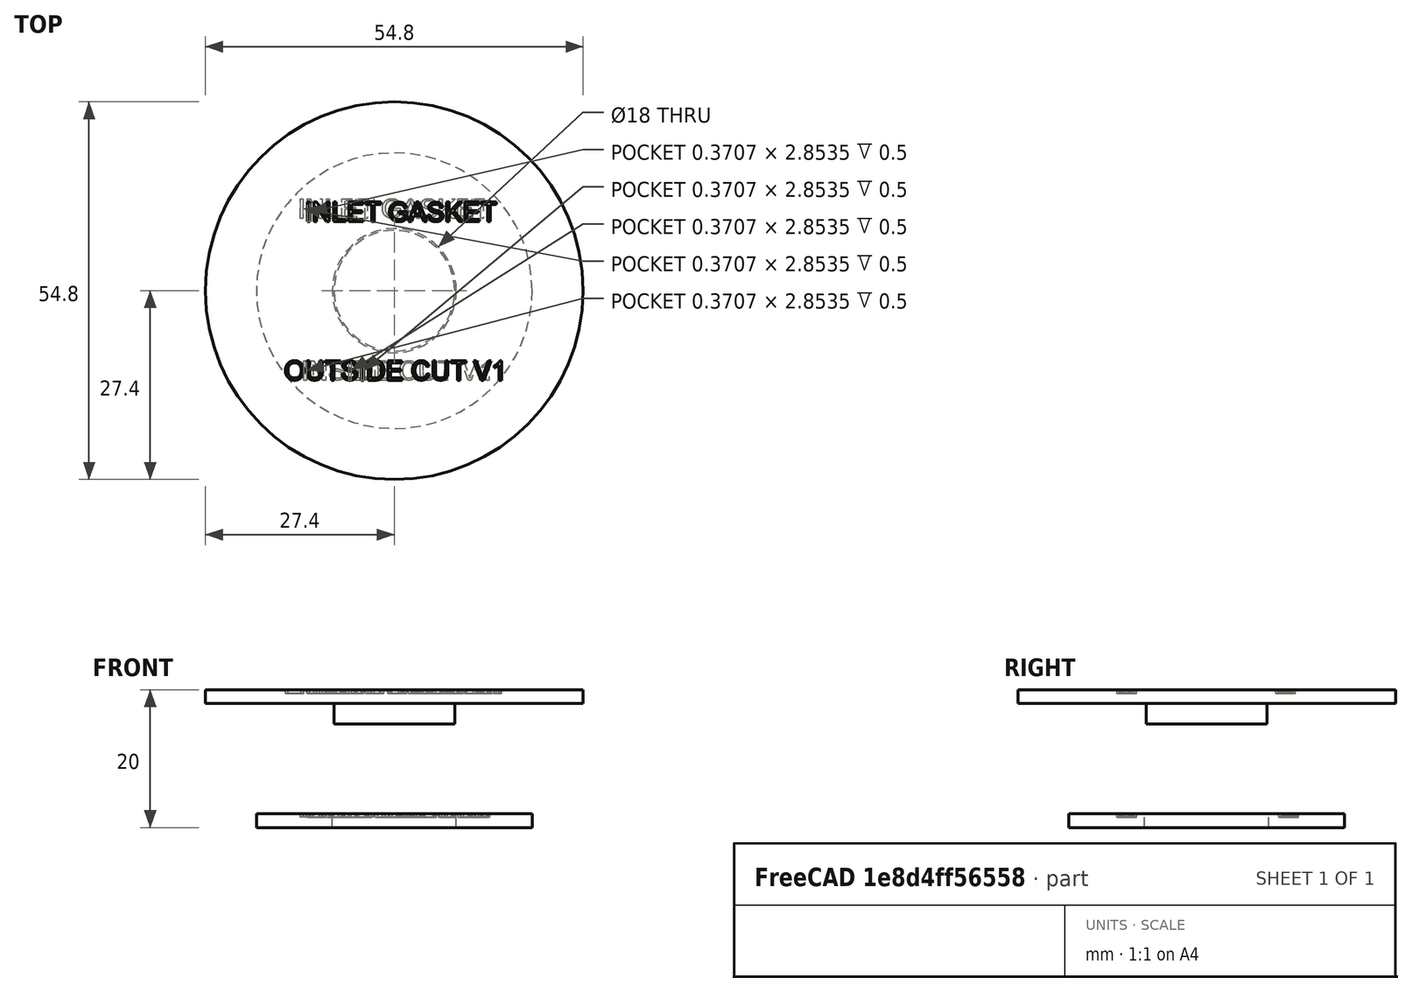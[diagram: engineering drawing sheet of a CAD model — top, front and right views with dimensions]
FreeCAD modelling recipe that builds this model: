
FCSTD DOCUMENT  (FreeCAD 0.18R4 (GitTag))
Label: InletGastketJigs
License: All rights reserved
LicenseURL: http://en.wikipedia.org/wiki/All_rights_reserved
objects: Part::Cylinder×4, Part::Part2DObjectPython×4, Part::Extrusion×4, Part::Cut×3, Part::MultiFuse×3
note: 18 computed .brp shape members not serialized (recipe doc carries the construction recipe); baked Part::Feature solids carry a one-line shape summary decoded from their .brp

FEATURE [Part::Cylinder] Cylinder
  Angle = 360
  AttacherType = Attacher::AttachEngine3D
  Height = 2
  Radius = 20
FEATURE [Part::Cylinder] Cylinder001
  Angle = 360
  AttacherType = Attacher::AttachEngine3D
  Height = 2
  Radius = 9
FEATURE [Part::Cut] Cut
  Base = -> Cylinder
  Tool = -> Cylinder001
FEATURE [Part::Part2DObjectPython] ShapeString  # Draft 2D object (typed FeaturePython)
  FontFile = <path>
  Size = 3
  String = INLET GASKET
  Tracking = 0
FEATURE [Part::Part2DObjectPython] ShapeString001  # Draft 2D object (typed FeaturePython)
  FontFile = <path>
  Size = 3
  String = INSIDE CUT V1
  Tracking = 0
FEATURE [Part::Extrusion] Extrude
  Base = -> ShapeString
  Dir = (0,0,1)
  DirMode = 2
  FaceMakerClass = Part::FaceMakerBullseye
  LengthFwd = 0.5
  LengthRev = 0
  Placement = pos=(-14,10.5,1.5) rot=(0,0,1;0rad)
  Solid = false
  Symmetric = false
FEATURE [Part::Extrusion] Extrude001
  Base = -> ShapeString001
  Dir = (0,0,1)
  DirMode = 2
  FaceMakerClass = Part::FaceMakerBullseye
  LengthFwd = 0.5
  LengthRev = 0
  Placement = pos=(-13.5,-13,1.5) rot=(0,0,1;0rad)
  Solid = false
  Symmetric = false
FEATURE [Part::MultiFuse] Fusion  label="words"
  Shapes = -> [Extrude,Extrude001]
FEATURE [Part::Cut] Cut001  label="InletGasketJigInsideV1"
  Base = -> Cut
  Tool = -> Fusion
FEATURE [Part::Cylinder] Cylinder002
  Angle = 360
  AttacherType = Attacher::AttachEngine3D
  Height = 2
  Radius = 27.4
FEATURE [Part::Cylinder] Cylinder003
  Angle = 360
  AttacherType = Attacher::AttachEngine3D
  Height = 5
  Radius = 8.75
FEATURE [Part::MultiFuse] Fusion001  label="InletGasketJigOutsideBody"
  Placement = pos=(0,2.4e-15,20) rot=(1,0,0;3.14159rad)
  Shapes = -> [Cylinder002,Cylinder003]
FEATURE [Part::Part2DObjectPython] ShapeString002  # Draft 2D object (typed FeaturePython)
  FontFile = <path>
  Size = 3
  String = INLET GASKET
  Tracking = 0
FEATURE [Part::Part2DObjectPython] ShapeString003  # Draft 2D object (typed FeaturePython)
  FontFile = <path>
  Size = 3
  String = OUTSIDE CUT V1
  Tracking = 0
FEATURE [Part::Extrusion] Extrude002
  Base = -> ShapeString002
  Dir = (0,0,1)
  DirMode = 2
  FaceMakerClass = Part::FaceMakerBullseye
  LengthFwd = 0.5
  LengthRev = 0
  Placement = pos=(-13,10,19.5) rot=(0,0,1;0rad)
  Solid = false
  Symmetric = false
FEATURE [Part::Extrusion] Extrude003
  Base = -> ShapeString003
  Dir = (0,0,1)
  DirMode = 2
  FaceMakerClass = Part::FaceMakerBullseye
  LengthFwd = 0.5
  LengthRev = 0
  Placement = pos=(-16,-13,19.5) rot=(0,0,1;0rad)
  Solid = false
  Symmetric = false
FEATURE [Part::MultiFuse] Fusion002  label="Words2"
  Shapes = -> [Extrude002,Extrude003]
FEATURE [Part::Cut] Cut002  label="InletGasketJigOutsideV1"
  Base = -> Fusion001
  Tool = -> Fusion002
note: 4 file-system paths scrubbed to <path> (originals preserved in the JSON sidecar)
